# Revit family: ВКПФ_Eng
name_source: partatom
category: Mechanical Equipment
units: mm (PartAtom-declared; Revit-internal decimal feet)

## family parameters
Always vertical = Yes
Classification = None
Cut with Voids When Loaded = No
Part Type = Normal
Room Calculation Point = No
Round Connector Dimension = Use Diameter
Shared = No
Work Plane-Based = No

## types (15) — shared parameters
00_20_Manufacturer = Vents
00_20_Name = Inline centrifugal fan
Casing Material = Steel, galvanized
Frequency = 50 Hz
Load Classification = HVAC
Maintenance zone material = <By Category>
Manufacturer = Vents
URL = https://ventilation-system.com
zero-valued in all types: Default Elevation

## per-type parameters (varying)
- VKPF 4E 400x200: Alfa=90.00°; Amperage=1 A; Apparent Load=304 VA; B=400 mm; Be=40 mm  [stored 0.131234 ft]; Electrical box=No; Frame=Frame : 400x200; H=200 mm  [stored 0.656168 ft]; He=0 mm  [stored 0 ft]; Height=200 mm  [stored 0.656168 ft]; L=500 mm; Length=500 mm; Maximum Air Flow=400.0 L/s; Number of Fase=1; Power=295 W; Voltage=230 V; Weight=17.50 kg; Width=400 mm; b=67 mm; b1=160 mm  [stored 0.524934 ft]; b11=200 mm  [stored 0.656168 ft]; b2=396 mm; b3=100 mm  [stored 0.328084 ft]; h=67 mm; h1=95 mm  [stored 0.31168 ft]; h2=198 mm  [stored 0.649606 ft]; h3=100 mm  [stored 0.328084 ft]; l=107 mm; l1=210 mm  [stored 0.688976 ft]; l3=150 mm  [stored 0.492126 ft]; r1=100 mm  [stored 0.328084 ft]; r2=80 mm  [stored 0.262467 ft]; r3=13 mm; Сonnector=Yes
- VKPF 4D 800x500: Alfa=0.00°; Amperage=9 A; Apparent Load=3740 VA; B=800 mm; Be=700 mm; Electrical box=Yes; Frame=Frame : 800x500; H=500 mm; He=25 mm  [stored 0.082021 ft]; Height=500 mm; L=820 mm; Length=820 mm; Maximum Air Flow=2256.0 L/s; Number of Fase=3; Power=5850 W; Voltage=400 V; Weight=74.00 kg; Width=800 mm; b=133 mm; b1=360 mm; b11=400 mm; b2=796 mm; b3=300 mm; h=167 mm; h1=238 mm; h2=498 mm; h3=250 mm  [stored 0.82021 ft]; l=176 mm; l1=370 mm; l3=310 mm; r1=250 mm  [stored 0.82021 ft]; r2=200 mm  [stored 0.656168 ft]; r3=33 mm  [stored 0.108268 ft]; Сonnector=No
- VKPF 4D 400x200: Alfa=90.00°; Amperage=1 A; Apparent Load=240 VA; B=400 mm; Be=40 mm  [stored 0.131234 ft]; Electrical box=No; Frame=Frame : 400x200; H=200 mm  [stored 0.656168 ft]; He=0 mm  [stored 0 ft]; Height=200 mm  [stored 0.656168 ft]; L=500 mm; Length=500 mm; Maximum Air Flow=408.0 L/s; Number of Fase=3; Power=282 W; Voltage=400 V; Weight=17.50 kg; Width=400 mm; b=67 mm; b1=160 mm  [stored 0.524934 ft]; b11=200 mm  [stored 0.656168 ft]; b2=396 mm; b3=100 mm  [stored 0.328084 ft]; h=67 mm; h1=95 mm  [stored 0.31168 ft]; h2=198 mm  [stored 0.649606 ft]; h3=100 mm  [stored 0.328084 ft]; l=107 mm; l1=210 mm  [stored 0.688976 ft]; l3=150 mm  [stored 0.492126 ft]; r1=100 mm  [stored 0.328084 ft]; r2=80 mm  [stored 0.262467 ft]; r3=13 mm; Сonnector=Yes
- VKPF 4E 500x300: Alfa=90.00°; Amperage=3 A; Apparent Load=713 VA; B=500 mm; Be=40 mm  [stored 0.131234 ft]; Electrical box=No; Frame=Frame : 500x300; H=300 mm; He=0 mm  [stored 0 ft]; Height=300 mm; L=680 mm; Length=680 mm; Maximum Air Flow=653.0 L/s; Number of Fase=1; Power=710 W; Voltage=230 V; Weight=33.00 kg; Width=500 mm; b=83 mm; b1=210 mm  [stored 0.688976 ft]; b11=250 mm  [stored 0.82021 ft]; b2=496 mm; b3=150 mm  [stored 0.492126 ft]; h=100 mm  [stored 0.328084 ft]; h1=143 mm; h2=298 mm; h3=150 mm  [stored 0.492126 ft]; l=146 mm; l1=300 mm; l3=240 mm  [stored 0.787402 ft]; r1=150 mm  [stored 0.492126 ft]; r2=120 mm  [stored 0.393701 ft]; r3=20 mm  [stored 0.0656168 ft]; Сonnector=Yes
- VKPF 4D 500x300: Alfa=90.00°; Amperage=2 A; Apparent Load=680 VA; B=500 mm; Be=40 mm  [stored 0.131234 ft]; Electrical box=No; Frame=Frame : 500x300; H=300 mm; He=0 mm  [stored 0 ft]; Height=300 mm; L=680 mm; Length=680 mm; Maximum Air Flow=653.0 L/s; Number of Fase=3; Power=855 W; Voltage=400 V; Weight=33.00 kg; Width=500 mm; b=83 mm; b1=210 mm  [stored 0.688976 ft]; b11=250 mm  [stored 0.82021 ft]; b2=496 mm; b3=150 mm  [stored 0.492126 ft]; h=100 mm  [stored 0.328084 ft]; h1=143 mm; h2=298 mm; h3=150 mm  [stored 0.492126 ft]; l=146 mm; l1=300 mm; l3=240 mm  [stored 0.787402 ft]; r1=150 mm  [stored 0.492126 ft]; r2=120 mm  [stored 0.393701 ft]; r3=20 mm  [stored 0.0656168 ft]; Сonnector=Yes
- VKPF 4E 600x300: Alfa=0.00°; Amperage=6 A; Apparent Load=1484 VA; B=600 mm; Be=500 mm; Electrical box=Yes; Frame=Frame : 600x300; H=300 mm; He=25 mm  [stored 0.082021 ft]; Height=300 mm; L=680 mm; Length=680 mm; Maximum Air Flow=820.0 L/s; Number of Fase=1; Power=1240 W; Voltage=230 V; Weight=35.00 kg; Width=600 mm; b=100 mm  [stored 0.328084 ft]; b1=260 mm; b11=300 mm; b2=596 mm; b3=200 mm  [stored 0.656168 ft]; h=100 mm  [stored 0.328084 ft]; h1=143 mm; h2=298 mm; h3=150 mm  [stored 0.492126 ft]; l=146 mm; l1=300 mm; l3=240 mm  [stored 0.787402 ft]; r1=150 mm  [stored 0.492126 ft]; r2=120 mm  [stored 0.393701 ft]; r3=20 mm  [stored 0.0656168 ft]; Сonnector=No
- VKPF 4D 600x300: Alfa=0.00°; Amperage=3 A; Apparent Load=1092 VA; B=600 mm; Be=500 mm; Electrical box=Yes; Frame=Frame : 600x300; H=300 mm; He=25 mm  [stored 0.082021 ft]; Height=300 mm; L=680 mm; Length=680 mm; Maximum Air Flow=1039.0 L/s; Number of Fase=3; Power=1560 W; Voltage=400 V; Weight=35.00 kg; Width=600 mm; b=100 mm  [stored 0.328084 ft]; b1=260 mm; b11=300 mm; b2=596 mm; b3=200 mm  [stored 0.656168 ft]; h=100 mm  [stored 0.328084 ft]; h1=143 mm; h2=298 mm; h3=150 mm  [stored 0.492126 ft]; l=146 mm; l1=300 mm; l3=240 mm  [stored 0.787402 ft]; r1=150 mm  [stored 0.492126 ft]; r2=120 mm  [stored 0.393701 ft]; r3=20 mm  [stored 0.0656168 ft]; Сonnector=No
- VKPF 4E 600x350: Alfa=0.00°; Amperage=14 A; Apparent Load=3197 VA; B=600 mm; Be=500 mm; Electrical box=Yes; Frame=Frame : 600x350; H=350 mm; He=25 mm  [stored 0.082021 ft]; Height=350 mm; L=735 mm; Length=735 mm; Maximum Air Flow=1183.0 L/s; Number of Fase=1; Power=2840 W; Voltage=230 V; Weight=49.50 kg; Width=600 mm; b=100 mm  [stored 0.328084 ft]; b1=260 mm; b11=300 mm; b2=596 mm; b3=200 mm  [stored 0.656168 ft]; h=117 mm; h1=167 mm; h2=348 mm; h3=175 mm  [stored 0.574147 ft]; l=158 mm  [stored 0.518373 ft]; l1=328 mm; l3=268 mm; r1=175 mm  [stored 0.574147 ft]; r2=140 mm  [stored 0.459318 ft]; r3=23 mm  [stored 0.0754593 ft]; Сonnector=No
- VKPF 4D 600x350: Alfa=0.00°; Amperage=4 A; Apparent Load=1572 VA; B=600 mm; Be=500 mm; Electrical box=Yes; Frame=Frame : 600x350; H=350 mm; He=25 mm  [stored 0.082021 ft]; Height=350 mm; L=735 mm; Length=735 mm; Maximum Air Flow=1395.0 L/s; Number of Fase=3; Power=2460 W; Voltage=400 V; Weight=49.50 kg; Width=600 mm; b=100 mm  [stored 0.328084 ft]; b1=260 mm; b11=300 mm; b2=596 mm; b3=200 mm  [stored 0.656168 ft]; h=117 mm; h1=167 mm; h2=348 mm; h3=175 mm  [stored 0.574147 ft]; l=158 mm  [stored 0.518373 ft]; l1=328 mm; l3=268 mm; r1=175 mm  [stored 0.574147 ft]; r2=140 mm  [stored 0.459318 ft]; r3=23 mm  [stored 0.0754593 ft]; Сonnector=No
- VKPF 4D 700x400: Alfa=0.00°; Amperage=6 A; Apparent Load=2400 VA; B=700 mm; Be=600 mm; Electrical box=Yes; Frame=Frame : 700x400; H=400 mm; He=25 mm  [stored 0.082021 ft]; Height=400 mm; L=780 mm; Length=780 mm; Maximum Air Flow=1792.0 L/s; Number of Fase=3; Power=3630 W; Voltage=400 V; Weight=60.00 kg; Width=700 mm; b=117 mm; b1=310 mm; b11=350 mm; b2=696 mm; b3=250 mm  [stored 0.82021 ft]; h=133 mm; h1=190 mm; h2=398 mm; h3=200 mm  [stored 0.656168 ft]; l=167 mm; l1=350 mm; l3=290 mm; r1=200 mm  [stored 0.656168 ft]; r2=160 mm  [stored 0.524934 ft]; r3=27 mm; Сonnector=No
- VKPF 4E 500x250: Alfa=90.00°; Amperage=2 A; Apparent Load=573 VA; B=500 mm; Be=40 mm  [stored 0.131234 ft]; Electrical box=No; Frame=Frame : 500x250; H=250 mm  [stored 0.82021 ft]; He=0 mm  [stored 0 ft]; Height=250 mm  [stored 0.82021 ft]; L=640 mm; Length=640 mm; Maximum Air Flow=486.0 L/s; Number of Fase=1; Power=535 W; Voltage=230 V; Weight=24.00 kg; Width=500 mm; b=83 mm; b1=210 mm  [stored 0.688976 ft]; b11=250 mm  [stored 0.82021 ft]; b2=496 mm; b3=150 mm  [stored 0.492126 ft]; h=83 mm; h1=119 mm; h2=248 mm  [stored 0.813648 ft]; h3=125 mm  [stored 0.410105 ft]; l=137 mm; l1=280 mm; l3=220 mm  [stored 0.721785 ft]; r1=125 mm  [stored 0.410105 ft]; r2=100 mm  [stored 0.328084 ft]; r3=17 mm  [stored 0.0557743 ft]; Сonnector=Yes
- VKPF 4D 500x250: Alfa=90.00°; Amperage=1 A; Apparent Load=376 VA; B=500 mm; Be=40 mm  [stored 0.131234 ft]; Electrical box=No; Frame=Frame : 500x250; H=250 mm  [stored 0.82021 ft]; He=0 mm  [stored 0 ft]; Height=250 mm  [stored 0.82021 ft]; L=640 mm; Length=640 mm; Maximum Air Flow=514.0 L/s; Number of Fase=3; Power=570 W; Voltage=400 V; Weight=24.00 kg; Width=500 mm; b=83 mm; b1=210 mm  [stored 0.688976 ft]; b11=250 mm  [stored 0.82021 ft]; b2=496 mm; b3=150 mm  [stored 0.492126 ft]; h=83 mm; h1=119 mm; h2=248 mm  [stored 0.813648 ft]; h3=125 mm  [stored 0.410105 ft]; l=137 mm; l1=280 mm; l3=220 mm  [stored 0.721785 ft]; r1=125 mm  [stored 0.410105 ft]; r2=100 mm  [stored 0.328084 ft]; r3=17 mm  [stored 0.0557743 ft]; Сonnector=Yes
- VKPF 6D 800x500: Alfa=0.00°; Amperage=5 A; Apparent Load=2072 VA; B=800 mm; Be=700 mm; Electrical box=Yes; Frame=Frame : 800x500; H=500 mm; He=25 mm  [stored 0.082021 ft]; Height=500 mm; L=820 mm; Length=820 mm; Maximum Air Flow=2114.0 L/s; Number of Fase=3; Power=2790 W; Voltage=400 V; Weight=70.00 kg; Width=800 mm; b=133 mm; b1=360 mm; b11=400 mm; b2=796 mm; b3=300 mm; h=167 mm; h1=238 mm; h2=498 mm; h3=250 mm  [stored 0.82021 ft]; l=176 mm; l1=370 mm; l3=310 mm; r1=250 mm  [stored 0.82021 ft]; r2=200 mm  [stored 0.656168 ft]; r3=33 mm  [stored 0.108268 ft]; Сonnector=No
- VKPF 6D 900x500: Alfa=0.00°; Amperage=7 A; Apparent Load=2800 VA; B=900 mm; Be=800 mm; Electrical box=Yes; Frame=Frame : 900x500; H=500 mm; He=25 mm  [stored 0.082021 ft]; Height=500 mm; L=954 mm; Length=954 mm; Maximum Air Flow=2650.0 L/s; Number of Fase=3; Power=3870 W; Voltage=400 V; Weight=90.00 kg; Width=900 mm; b=150 mm  [stored 0.492126 ft]; b1=410 mm; b11=450 mm; b2=896 mm; b3=350 mm; h=167 mm; h1=238 mm; h2=498 mm; h3=250 mm  [stored 0.82021 ft]; l=204 mm  [stored 0.669291 ft]; l1=437 mm; l3=377 mm; r1=250 mm  [stored 0.82021 ft]; r2=200 mm  [stored 0.656168 ft]; r3=33 mm  [stored 0.108268 ft]; Сonnector=No
- VKPF 6D 1000x500: Alfa=0.00°; Amperage=7 A; Apparent Load=2800 VA; B=1000 mm; Be=900 mm; Electrical box=Yes; Frame=Frame : 1000x500; H=500 mm; He=25 mm  [stored 0.082021 ft]; Height=500 mm; L=954 mm; Length=954 mm; Maximum Air Flow=2650.0 L/s; Number of Fase=3; Power=3870 W; Voltage=400 V; Weight=95.00 kg; Width=1000 mm; b=167 mm; b1=460 mm; b11=500 mm; b2=996 mm; b3=400 mm; h=167 mm; h1=238 mm; h2=498 mm; h3=250 mm  [stored 0.82021 ft]; l=204 mm  [stored 0.669291 ft]; l1=437 mm; l3=377 mm; r1=250 mm  [stored 0.82021 ft]; r2=200 mm  [stored 0.656168 ft]; r3=33 mm  [stored 0.108268 ft]; Сonnector=No

note: column(s) folded — value = type name in every type: 00_20_Type

note: [stored X ft] marks values corroborated as IEEE doubles in the binary element streams (Revit-internal decimal feet)
